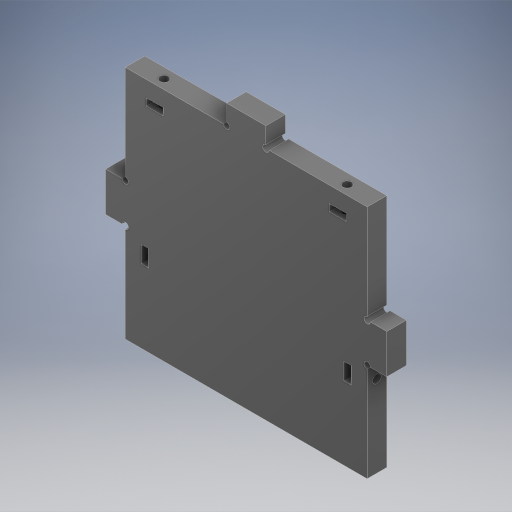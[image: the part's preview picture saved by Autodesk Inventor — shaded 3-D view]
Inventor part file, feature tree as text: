
AUTODESK INVENTOR PART (.ipt)
format: ipt  version: 2024 (Build 280153000, 153)  size: 362,496 bytes
history: native  units: in
note: dims shown in document units (in); Inventor stores cm internally (conversion verified against a paired STEP export)
features: reference x13, extrude x6, sketch x6, other x5, projected_geometry x1
ambient origin geometry x8: Origin, YZ Plane, XZ Plane, XY Plane, X Axis, Y Axis, Z Axis, Center Point
bodies: Body1 (feature_tree)
feature tree (31):
  other  "솔리드1"
  extrude  "돌출1"  Depth=0.4724in
  extrude  "돌출2"  Depth=0.2362in
  extrude  "돌출3"  Depth=0.2362in
  extrude  "돌출4"  Depth=0.4724in
  extrude  "돌출5"  Depth=0.2362in
  extrude  "돌출6"  Depth=0.4724in
  sketch  "스케치1"
  reference  "참조1"
  reference  "참조2"
  reference  "참조3"
  reference  "참조4"
  reference  "참조5"
  reference  "참조6"
  reference  "참조7"
  reference  "참조8"
  reference  "참조9"
  sketch  "스케치2"
  reference  "참조10"
  reference  "참조11"
  sketch  "스케치3"
  reference  "참조12"
  sketch  "스케치4"
  reference  "참조13"
  sketch  "스케치5"
  sketch  "스케치6"
  projected_geometry  "투영된 루프1"
  other  "조립품5"
  other  "head:1"
  other  "body_top:2"
  other  "body_top:1"
